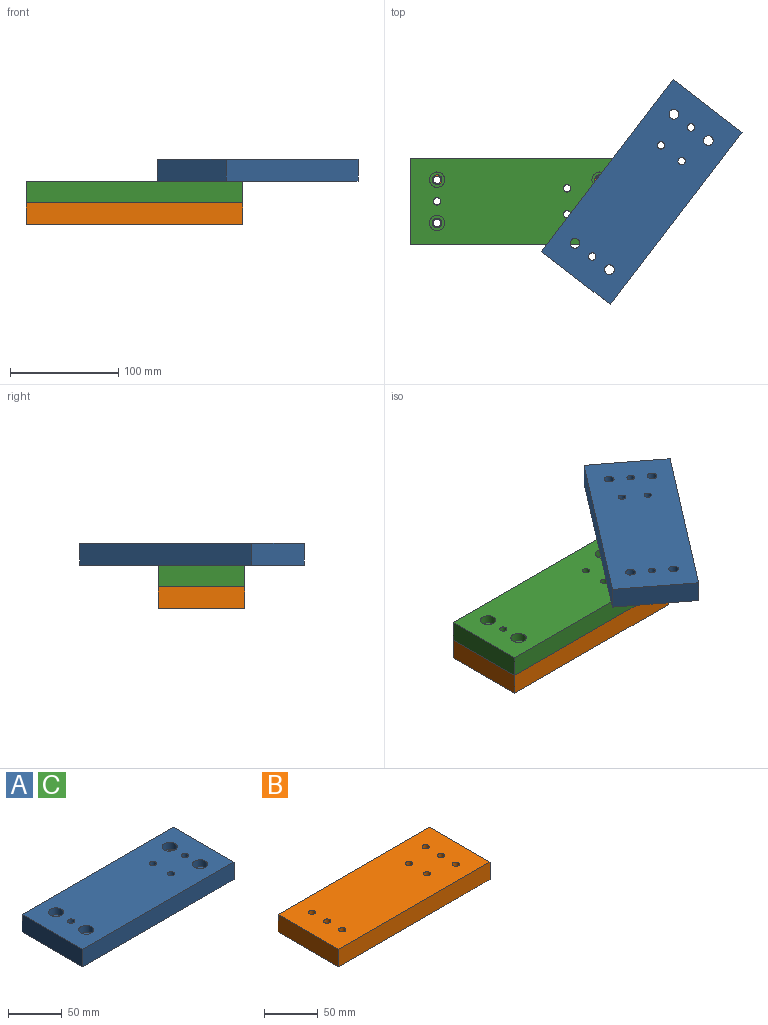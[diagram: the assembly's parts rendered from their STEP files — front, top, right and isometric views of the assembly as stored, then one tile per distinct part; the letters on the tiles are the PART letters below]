
ASSEMBLY  parts=3 mates=3
PART A: 22 faces, bbox 200x80x20 mm
  f0: plane 200x20mm, normal (0,-1,0), area 4000mm2, adj f1,f3,f4,f5
  f1: plane 80x20mm, normal (1,0,0), area 1600mm2, adj f0,f2,f4,f5
  f2: plane 200x20mm, normal (0,1,0), area 4000mm2, adj f1,f3,f4,f5
  f3: plane 80x20mm, normal (-1,0,0), area 1600mm2, adj f0,f2,f4,f5
  f4: plane 200x80mm, normal (0,0,1), area 15216.8mm2, adj f0,f1,f2,f3,f8,f11,f14,f17
  f5: plane 200x80mm, normal (0,0,-1), area 15600.3mm2, adj f0,f1,f2,f3,f6,f9,f12,f15
  f6: cylinder r=4.5mm len=12mm, axis (0,0,1), area 339.3mm2, adj f5,f7
  f7: plane 14.25x14.25mm, normal (0,0,1), area 95.9mm2, adj f6,f8
  f8: cylinder r=7.12mm len=14.25mm, axis (0,0,1), area 358.1mm2, adj f4,f7
  f9: cylinder r=4.5mm len=12mm, axis (0,0,1), area 339.3mm2, adj f5,f10
  f10: plane 14.25x14.25mm, normal (0,0,1), area 95.9mm2, adj f9,f11
  f11: cylinder r=7.12mm len=14.25mm, axis (0,0,1), area 358.1mm2, adj f4,f10
  f12: cylinder r=4.5mm len=12mm, axis (0,0,1), area 339.3mm2, adj f5,f13
  f13: plane 14.25x14.25mm, normal (0,0,1), area 95.9mm2, adj f12,f14
  f14: cylinder r=7.12mm len=14.25mm, axis (0,0,1), area 358.1mm2, adj f4,f13
  f15: cylinder r=4.5mm len=12mm, axis (0,0,1), area 339.3mm2, adj f5,f16
  f16: plane 14.25x14.25mm, normal (0,0,1), area 95.9mm2, adj f15,f17
  f17: cylinder r=7.12mm len=14.25mm, axis (0,0,1), area 358.1mm2, adj f4,f16
  f18: cylinder r=3.4mm len=20mm, axis (0,0,1), area 427.3mm2, adj f4,f5
  f19: cylinder r=3.4mm len=20mm, axis (0,0,1), area 427.3mm2, adj f4,f5
  f20: cylinder r=3.4mm len=20mm, axis (0,0,1), area 427.3mm2, adj f4,f5
  f21: cylinder r=3.4mm len=20mm, axis (0,0,1), area 427.3mm2, adj f4,f5
PART B: 14 faces, bbox 200x80x20 mm
  f0: plane 200x20mm, normal (0,-1,0), area 4000mm2, adj f1,f3,f4,f5
  f1: plane 80x20mm, normal (1,0,0), area 1600mm2, adj f0,f2,f4,f5
  f2: plane 200x20mm, normal (0,1,0), area 4000mm2, adj f1,f3,f4,f5
  f3: plane 80x20mm, normal (-1,0,0), area 1600mm2, adj f0,f2,f4,f5
  f4: plane 200x80mm, normal (0,0,1), area 15709.5mm2, adj f0,f1,f2,f3,f6,f7,f8,f9
  f5: plane 200x80mm, normal (0,0,-1), area 15709.5mm2, adj f0,f1,f2,f3,f6,f7,f8,f9
  f6: cylinder r=3.4mm len=20mm, axis (0,0,1), area 427.3mm2, adj f4,f5
  f7: cylinder r=3.4mm len=20mm, axis (0,0,1), area 427.3mm2, adj f4,f5
  f8: cylinder r=3.4mm len=20mm, axis (0,0,1), area 427.3mm2, adj f4,f5
  f9: cylinder r=3.4mm len=20mm, axis (0,0,1), area 427.3mm2, adj f4,f5
  f10: cylinder r=3.4mm len=20mm, axis (0,0,1), area 427.3mm2, adj f4,f5
  f11: cylinder r=3.4mm len=20mm, axis (0,0,1), area 427.3mm2, adj f4,f5
  f12: cylinder r=3.4mm len=20mm, axis (0,0,1), area 427.3mm2, adj f4,f5
  f13: cylinder r=3.4mm len=20mm, axis (0,0,1), area 427.3mm2, adj f4,f5
PART C: same geometry as A
PLACE A rot(axis=(0.9,0.44,0),180deg) t=(122.85,24.05,46.57)mm
PLACE B t=(9.12,15.41,-13.43)mm
PLACE C t=(9.12,15.41,6.57)mm fixed
MATE planar B.f1 <-> C.f1  axis (1,0,0) through (109.12,15.41,-3.43)mm
MATE parallel A.f5 <-> C.f20  axis (0,0,1) through (122.72,23.88,46.57)mm
MATE planar C.f4 <-> A.f4  axis (0,0,1) through (9.12,-24.59,26.57)mm
